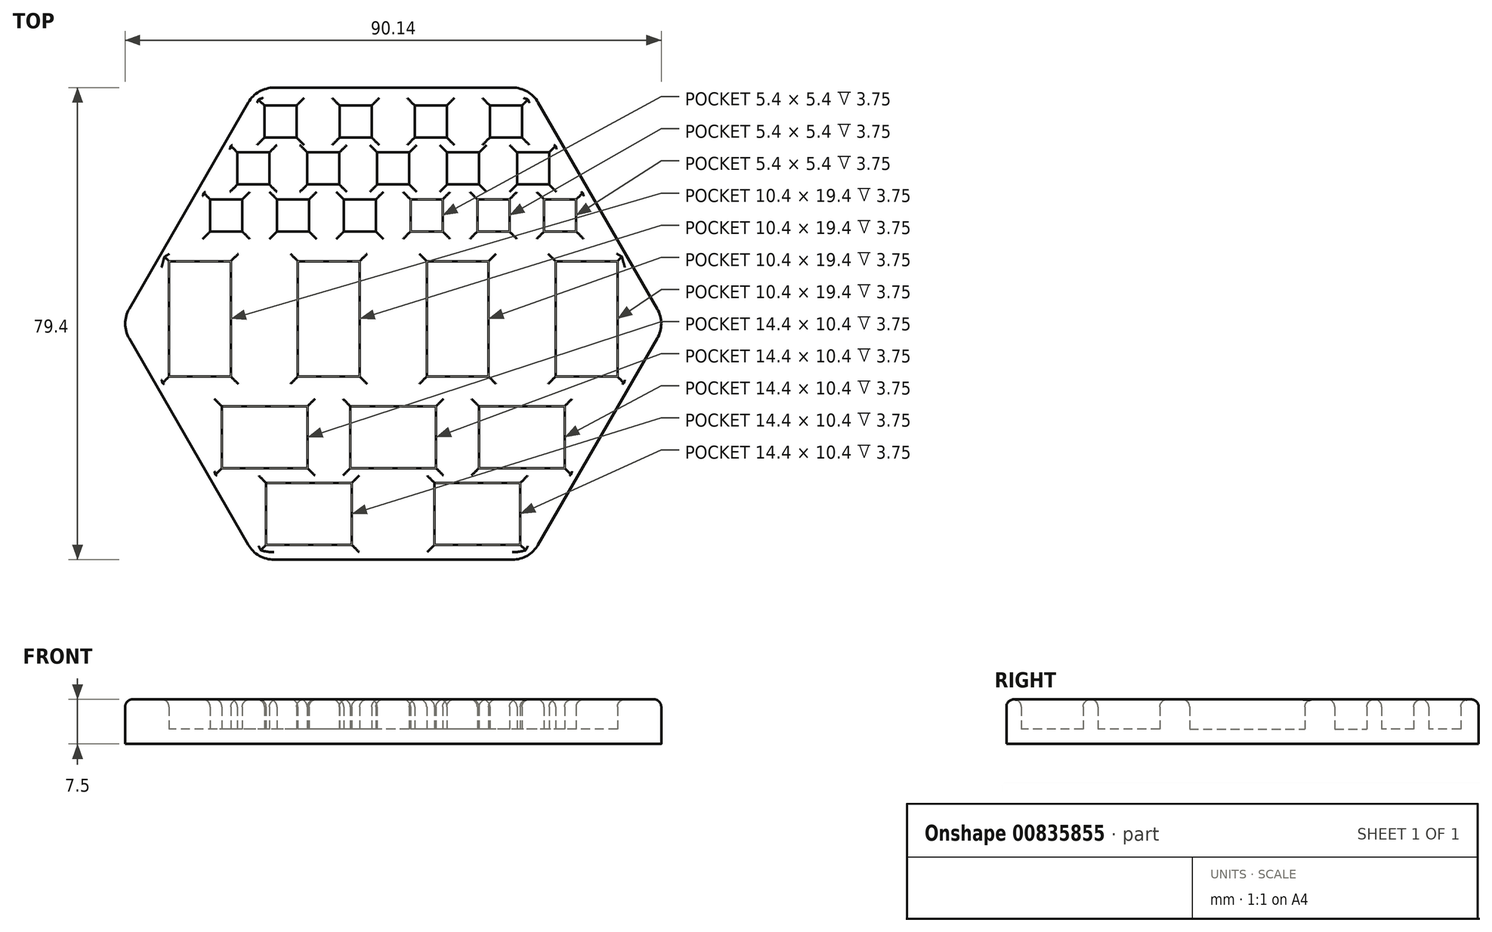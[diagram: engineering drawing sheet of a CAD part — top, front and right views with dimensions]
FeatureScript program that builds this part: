
annotation { "Feature Type Name" : "Feature", "Feature Type Description" : "" }
export const myFeature = defineFeature(function(context is Context, id is Id, definition is map)
    precondition{}
    {
        {
            var Q0;
            Q0=qCreatedBy(makeId("Top.planeOp"),FACE);
            var sketch = newSketch(context, id + "F0", { "sketchPlane" : qUnion([Q0])});
            skCircle(sketch, "E0.cCircle", {"center": v(0, 0) * mm, "radius": 39.7 * mm, "construction": true});
            skLineSegment(sketch, "E0.0", {"start": v(22.92, 39.7) * mm, "end": v(45.84, 0) * mm});
            skLineSegment(sketch, "E0.1", {"start": v(45.84, 0) * mm, "end": v(22.92, -39.7) * mm});
            skLineSegment(sketch, "E0.2", {"start": v(22.92, -39.7) * mm, "end": v(-22.92, -39.7) * mm});
            skLineSegment(sketch, "E0.3", {"start": v(-22.92, -39.7) * mm, "end": v(-45.84, 0) * mm});
            skLineSegment(sketch, "E0.4", {"start": v(-45.84, 0) * mm, "end": v(-22.92, 39.7) * mm});
            skLineSegment(sketch, "E0.5", {"start": v(-22.92, 39.7) * mm, "end": v(22.92, 39.7) * mm});
            skPoint(sketch, "E0.0.midPoint", {"position": v(34.38, 19.85) * mm});
            skLineSegment(sketch, "E1.bottom", {"start": v(-16.25, 36.7) * mm, "end": v(-21.65, 36.7) * mm});
            skLineSegment(sketch, "E1.top", {"start": v(-16.25, 31.3) * mm, "end": v(-21.65, 31.3) * mm});
            skLineSegment(sketch, "E1.left", {"start": v(-16.25, 36.7) * mm, "end": v(-16.25, 31.3) * mm});
            skLineSegment(sketch, "E1.right", {"start": v(-21.65, 36.7) * mm, "end": v(-21.65, 31.3) * mm});
            skPoint(sketch, "E1.middle", {"position": v(-18.95, 34) * mm});
            skLineSegment(sketch, "E2", {"start": v(-21.65, 36.7) * mm, "end": v(-24.65, 36.7) * mm, "construction": true});
            skLineSegment(sketch, "E3.1.0.0", {"start": v(-3.62, 31.3) * mm, "end": v(-9.02, 31.3) * mm});
            skLineSegment(sketch, "E3.1.0.1", {"start": v(-3.62, 36.7) * mm, "end": v(-3.62, 31.3) * mm});
            skLineSegment(sketch, "E3.1.0.2", {"start": v(-3.62, 36.7) * mm, "end": v(-9.02, 36.7) * mm});
            skLineSegment(sketch, "E3.1.0.3", {"start": v(-9.02, 36.7) * mm, "end": v(-9.02, 31.3) * mm});
            skLineSegment(sketch, "E3.2.0.0", {"start": v(9.02, 31.3) * mm, "end": v(3.62, 31.3) * mm});
            skLineSegment(sketch, "E3.2.0.1", {"start": v(9.02, 36.7) * mm, "end": v(9.02, 31.3) * mm});
            skLineSegment(sketch, "E3.2.0.2", {"start": v(9.02, 36.7) * mm, "end": v(3.62, 36.7) * mm});
            skLineSegment(sketch, "E3.2.0.3", {"start": v(3.62, 36.7) * mm, "end": v(3.62, 31.3) * mm});
            skLineSegment(sketch, "E3.3.0.0", {"start": v(21.65, 31.3) * mm, "end": v(16.25, 31.3) * mm});
            skLineSegment(sketch, "E3.3.0.1", {"start": v(21.65, 36.7) * mm, "end": v(21.65, 31.3) * mm});
            skLineSegment(sketch, "E3.3.0.2", {"start": v(21.65, 36.7) * mm, "end": v(16.25, 36.7) * mm});
            skLineSegment(sketch, "E3.3.0.3", {"start": v(16.25, 36.7) * mm, "end": v(16.25, 31.3) * mm});
            skLineSegment(sketch, "E3.direction1", {"start": v(-21.65, 31.3) * mm, "end": v(-9.02, 31.3) * mm, "construction": true});
            skLineSegment(sketch, "E4", {"start": v(21.65, 36.7) * mm, "end": v(24.65, 36.7) * mm, "construction": true});
            skLineSegment(sketch, "E5.bottom", {"start": v(-20.81, 28.8) * mm, "end": v(-26.21, 28.8) * mm});
            skLineSegment(sketch, "E5.top", {"start": v(-20.81, 23.4) * mm, "end": v(-26.21, 23.4) * mm});
            skLineSegment(sketch, "E5.left", {"start": v(-20.81, 28.8) * mm, "end": v(-20.81, 23.4) * mm});
            skLineSegment(sketch, "E5.right", {"start": v(-26.21, 28.8) * mm, "end": v(-26.21, 23.4) * mm});
            skPoint(sketch, "E5.middle", {"position": v(-23.51, 26.1) * mm});
            skLineSegment(sketch, "E6", {"start": v(-26.21, 28.8) * mm, "end": v(-29.21, 28.8) * mm, "construction": true});
            skLineSegment(sketch, "E7.1.0.0", {"start": v(-14.46, 28.8) * mm, "end": v(-14.46, 23.4) * mm});
            skLineSegment(sketch, "E7.1.0.1", {"start": v(-9.06, 28.8) * mm, "end": v(-14.46, 28.8) * mm});
            skLineSegment(sketch, "E7.1.0.2", {"start": v(-9.06, 28.8) * mm, "end": v(-9.06, 23.4) * mm});
            skLineSegment(sketch, "E7.1.0.3", {"start": v(-9.06, 23.4) * mm, "end": v(-14.46, 23.4) * mm});
            skLineSegment(sketch, "E7.2.0.0", {"start": v(-2.7, 28.8) * mm, "end": v(-2.7, 23.4) * mm});
            skLineSegment(sketch, "E7.2.0.1", {"start": v(2.7, 28.8) * mm, "end": v(-2.7, 28.8) * mm});
            skLineSegment(sketch, "E7.2.0.2", {"start": v(2.7, 28.8) * mm, "end": v(2.7, 23.4) * mm});
            skLineSegment(sketch, "E7.2.0.3", {"start": v(2.7, 23.4) * mm, "end": v(-2.7, 23.4) * mm});
            skLineSegment(sketch, "E7.3.0.0", {"start": v(9.06, 28.8) * mm, "end": v(9.06, 23.4) * mm});
            skLineSegment(sketch, "E7.3.0.1", {"start": v(14.46, 28.8) * mm, "end": v(9.06, 28.8) * mm});
            skLineSegment(sketch, "E7.3.0.2", {"start": v(14.46, 28.8) * mm, "end": v(14.46, 23.4) * mm});
            skLineSegment(sketch, "E7.3.0.3", {"start": v(14.46, 23.4) * mm, "end": v(9.06, 23.4) * mm});
            skLineSegment(sketch, "E7.4.0.0", {"start": v(20.81, 28.8) * mm, "end": v(20.81, 23.4) * mm});
            skLineSegment(sketch, "E7.4.0.1", {"start": v(26.21, 28.8) * mm, "end": v(20.81, 28.8) * mm});
            skLineSegment(sketch, "E7.4.0.2", {"start": v(26.21, 28.8) * mm, "end": v(26.21, 23.4) * mm});
            skLineSegment(sketch, "E7.4.0.3", {"start": v(26.21, 23.4) * mm, "end": v(20.81, 23.4) * mm});
            skLineSegment(sketch, "E7.direction1", {"start": v(-26.21, 23.4) * mm, "end": v(-14.46, 23.4) * mm, "construction": true});
            skLineSegment(sketch, "E8", {"start": v(26.21, 28.8) * mm, "end": v(29.21, 28.8) * mm, "construction": true});
            skLineSegment(sketch, "E9.bottom", {"start": v(-25.37, 15.5) * mm, "end": v(-30.77, 15.5) * mm});
            skLineSegment(sketch, "E9.top", {"start": v(-25.37, 20.9) * mm, "end": v(-30.77, 20.9) * mm});
            skLineSegment(sketch, "E9.left", {"start": v(-25.37, 15.5) * mm, "end": v(-25.37, 20.9) * mm});
            skLineSegment(sketch, "E9.right", {"start": v(-30.77, 15.5) * mm, "end": v(-30.77, 20.9) * mm});
            skPoint(sketch, "E9.middle", {"position": v(-28.07, 18.2) * mm});
            skLineSegment(sketch, "E10", {"start": v(-30.77, 20.9) * mm, "end": v(-33.77, 20.9) * mm, "construction": true});
            skLineSegment(sketch, "E11.1.0.0", {"start": v(-14.14, 20.9) * mm, "end": v(-19.54, 20.9) * mm});
            skLineSegment(sketch, "E11.1.0.1", {"start": v(-19.54, 15.5) * mm, "end": v(-19.54, 20.9) * mm});
            skLineSegment(sketch, "E11.1.0.2", {"start": v(-14.14, 15.5) * mm, "end": v(-19.54, 15.5) * mm});
            skLineSegment(sketch, "E11.1.0.3", {"start": v(-14.14, 15.5) * mm, "end": v(-14.14, 20.9) * mm});
            skLineSegment(sketch, "E11.2.0.0", {"start": v(-2.91, 20.9) * mm, "end": v(-8.31, 20.9) * mm});
            skLineSegment(sketch, "E11.2.0.1", {"start": v(-8.31, 15.5) * mm, "end": v(-8.31, 20.9) * mm});
            skLineSegment(sketch, "E11.2.0.2", {"start": v(-2.91, 15.5) * mm, "end": v(-8.31, 15.5) * mm});
            skLineSegment(sketch, "E11.2.0.3", {"start": v(-2.91, 15.5) * mm, "end": v(-2.91, 20.9) * mm});
            skLineSegment(sketch, "E11.3.0.0", {"start": v(8.31, 20.9) * mm, "end": v(2.91, 20.9) * mm});
            skLineSegment(sketch, "E11.3.0.1", {"start": v(2.91, 15.5) * mm, "end": v(2.91, 20.9) * mm});
            skLineSegment(sketch, "E11.3.0.2", {"start": v(8.31, 15.5) * mm, "end": v(2.91, 15.5) * mm});
            skLineSegment(sketch, "E11.3.0.3", {"start": v(8.31, 15.5) * mm, "end": v(8.31, 20.9) * mm});
            skLineSegment(sketch, "E11.4.0.0", {"start": v(19.54, 20.9) * mm, "end": v(14.14, 20.9) * mm});
            skLineSegment(sketch, "E11.4.0.1", {"start": v(14.14, 15.5) * mm, "end": v(14.14, 20.9) * mm});
            skLineSegment(sketch, "E11.4.0.2", {"start": v(19.54, 15.5) * mm, "end": v(14.14, 15.5) * mm});
            skLineSegment(sketch, "E11.4.0.3", {"start": v(19.54, 15.5) * mm, "end": v(19.54, 20.9) * mm});
            skLineSegment(sketch, "E11.5.0.0", {"start": v(30.77, 20.9) * mm, "end": v(25.37, 20.9) * mm});
            skLineSegment(sketch, "E11.5.0.1", {"start": v(25.37, 15.5) * mm, "end": v(25.37, 20.9) * mm});
            skLineSegment(sketch, "E11.5.0.2", {"start": v(30.77, 15.5) * mm, "end": v(25.37, 15.5) * mm});
            skLineSegment(sketch, "E11.5.0.3", {"start": v(30.77, 15.5) * mm, "end": v(30.77, 20.9) * mm});
            skLineSegment(sketch, "E11.direction1", {"start": v(-30.77, 20.9) * mm, "end": v(-19.54, 20.9) * mm, "construction": true});
            skLineSegment(sketch, "E12", {"start": v(30.77, 20.9) * mm, "end": v(33.77, 20.9) * mm, "construction": true});
            skLineSegment(sketch, "E13.bottom", {"start": v(-27.3, -8.9) * mm, "end": v(-37.7, -8.9) * mm});
            skLineSegment(sketch, "E13.top", {"start": v(-27.3, 10.5) * mm, "end": v(-37.7, 10.5) * mm});
            skLineSegment(sketch, "E13.left", {"start": v(-27.3, -8.9) * mm, "end": v(-27.3, 10.5) * mm});
            skLineSegment(sketch, "E13.right", {"start": v(-37.7, -8.9) * mm, "end": v(-37.7, 10.5) * mm});
            skPoint(sketch, "E13.middle", {"position": v(-32.5, 0.8) * mm});
            skLineSegment(sketch, "E14", {"start": v(-37.7, -8.9) * mm, "end": v(-40.7, -8.9) * mm, "construction": true});
            skLineSegment(sketch, "E15.1.0.0", {"start": v(-5.63, 10.5) * mm, "end": v(-16.03, 10.5) * mm});
            skLineSegment(sketch, "E15.1.0.1", {"start": v(-5.63, -8.9) * mm, "end": v(-5.63, 10.5) * mm});
            skLineSegment(sketch, "E15.1.0.2", {"start": v(-5.63, -8.9) * mm, "end": v(-16.03, -8.9) * mm});
            skLineSegment(sketch, "E15.1.0.3", {"start": v(-16.03, -8.9) * mm, "end": v(-16.03, 10.5) * mm});
            skLineSegment(sketch, "E15.2.0.0", {"start": v(16.03, 10.5) * mm, "end": v(5.63, 10.5) * mm});
            skLineSegment(sketch, "E15.2.0.1", {"start": v(16.03, -8.9) * mm, "end": v(16.03, 10.5) * mm});
            skLineSegment(sketch, "E15.2.0.2", {"start": v(16.03, -8.9) * mm, "end": v(5.63, -8.9) * mm});
            skLineSegment(sketch, "E15.2.0.3", {"start": v(5.63, -8.9) * mm, "end": v(5.63, 10.5) * mm});
            skLineSegment(sketch, "E15.3.0.0", {"start": v(37.7, 10.5) * mm, "end": v(27.3, 10.5) * mm});
            skLineSegment(sketch, "E15.3.0.1", {"start": v(37.7, -8.9) * mm, "end": v(37.7, 10.5) * mm});
            skLineSegment(sketch, "E15.3.0.2", {"start": v(37.7, -8.9) * mm, "end": v(27.3, -8.9) * mm});
            skLineSegment(sketch, "E15.3.0.3", {"start": v(27.3, -8.9) * mm, "end": v(27.3, 10.5) * mm});
            skLineSegment(sketch, "E15.direction1", {"start": v(-37.7, 10.5) * mm, "end": v(-16.03, 10.5) * mm, "construction": true});
            skLineSegment(sketch, "E16", {"start": v(37.7, -8.9) * mm, "end": v(40.7, -8.9) * mm, "construction": true});
            skLineSegment(sketch, "E17.bottom", {"start": v(-14.41, -13.9) * mm, "end": v(-28.81, -13.9) * mm});
            skLineSegment(sketch, "E17.top", {"start": v(-14.41, -24.3) * mm, "end": v(-28.81, -24.3) * mm});
            skLineSegment(sketch, "E17.left", {"start": v(-14.41, -13.9) * mm, "end": v(-14.41, -24.3) * mm});
            skLineSegment(sketch, "E17.right", {"start": v(-28.81, -13.9) * mm, "end": v(-28.81, -24.3) * mm});
            skPoint(sketch, "E17.middle", {"position": v(-21.61, -19.1) * mm});
            skLineSegment(sketch, "E18", {"start": v(-28.81, -24.3) * mm, "end": v(-31.81, -24.3) * mm, "construction": true});
            skLineSegment(sketch, "E19.1.0.0", {"start": v(7.2, -24.3) * mm, "end": v(-7.2, -24.3) * mm});
            skLineSegment(sketch, "E19.1.0.1", {"start": v(-7.2, -13.9) * mm, "end": v(-7.2, -24.3) * mm});
            skLineSegment(sketch, "E19.1.0.2", {"start": v(7.2, -13.9) * mm, "end": v(-7.2, -13.9) * mm});
            skLineSegment(sketch, "E19.1.0.3", {"start": v(7.2, -13.9) * mm, "end": v(7.2, -24.3) * mm});
            skLineSegment(sketch, "E19.2.0.0", {"start": v(28.81, -24.3) * mm, "end": v(14.41, -24.3) * mm});
            skLineSegment(sketch, "E19.2.0.1", {"start": v(14.41, -13.9) * mm, "end": v(14.41, -24.3) * mm});
            skLineSegment(sketch, "E19.2.0.2", {"start": v(28.81, -13.9) * mm, "end": v(14.41, -13.9) * mm});
            skLineSegment(sketch, "E19.2.0.3", {"start": v(28.81, -13.9) * mm, "end": v(28.81, -24.3) * mm});
            skLineSegment(sketch, "E19.direction1", {"start": v(-28.81, -24.3) * mm, "end": v(-7.2, -24.3) * mm, "construction": true});
            skLineSegment(sketch, "E20", {"start": v(28.81, -24.3) * mm, "end": v(31.81, -24.3) * mm, "construction": true});
            skLineSegment(sketch, "E21.bottom", {"start": v(-6.96, -26.8) * mm, "end": v(-21.36, -26.8) * mm});
            skLineSegment(sketch, "E21.top", {"start": v(-6.96, -37.2) * mm, "end": v(-21.36, -37.2) * mm});
            skLineSegment(sketch, "E21.left", {"start": v(-6.96, -26.8) * mm, "end": v(-6.96, -37.2) * mm});
            skLineSegment(sketch, "E21.right", {"start": v(-21.36, -26.8) * mm, "end": v(-21.36, -37.2) * mm});
            skPoint(sketch, "E21.middle", {"position": v(-14.16, -32) * mm});
            skLineSegment(sketch, "E22", {"start": v(-21.36, -37.2) * mm, "end": v(-24.36, -37.2) * mm, "construction": true});
            skLineSegment(sketch, "E23.1.0.0", {"start": v(6.96, -26.8) * mm, "end": v(6.96, -37.2) * mm});
            skLineSegment(sketch, "E23.1.0.1", {"start": v(21.36, -26.8) * mm, "end": v(6.96, -26.8) * mm});
            skLineSegment(sketch, "E23.1.0.2", {"start": v(21.36, -26.8) * mm, "end": v(21.36, -37.2) * mm});
            skLineSegment(sketch, "E23.1.0.3", {"start": v(21.36, -37.2) * mm, "end": v(6.96, -37.2) * mm});
            skLineSegment(sketch, "E23.direction1", {"start": v(-21.36, -37.2) * mm, "end": v(6.96, -37.2) * mm, "construction": true});
            skLineSegment(sketch, "E24", {"start": v(21.36, -37.2) * mm, "end": v(24.36, -37.2) * mm, "construction": true});
            skSolve(sketch);
        }
        {
            var Q0;
            Q0=makeQuery(id+"F0.imprint","IMPRINT",FACE,{"disambiguationData":[TD([[makeQuery(id+"F0.imprint","IMPRINT",EDGE,{"derivedFrom":sQuery(id+"F0.wireOp",EDGE,"E0.0")}),-1.0]])]});
            extrude(context, id + "F1", {"entities" : qUnion([Q0]), "depth" : 7.5 * mm, "offsetDistance" : 25 * mm});
        }
        {
            var Q0;
            Q0=makeQuery(id+"F0.imprint","IMPRINT",FACE,{"disambiguationData":[TD([[makeQuery(id+"F0.imprint","IMPRINT",EDGE,{"derivedFrom":sQuery(id+"F0.wireOp",EDGE,"E13.bottom")}),-1.0]])]});
            var Q1;
            Q1=makeQuery(id+"F0.imprint","IMPRINT",FACE,{"disambiguationData":[TD([[makeQuery(id+"F0.imprint","IMPRINT",EDGE,{"derivedFrom":sQuery(id+"F0.wireOp",EDGE,"E15.1.0.0")}),1.0]])]});
            var Q2;
            Q2=makeQuery(id+"F0.imprint","IMPRINT",FACE,{"disambiguationData":[TD([[makeQuery(id+"F0.imprint","IMPRINT",EDGE,{"derivedFrom":sQuery(id+"F0.wireOp",EDGE,"E15.2.0.0")}),1.0]])]});
            var Q3;
            Q3=makeQuery(id+"F0.imprint","IMPRINT",FACE,{"disambiguationData":[TD([[makeQuery(id+"F0.imprint","IMPRINT",EDGE,{"derivedFrom":sQuery(id+"F0.wireOp",EDGE,"E15.3.0.0")}),1.0]])]});
            var Q4;
            Q4=makeQuery(id+"F0.imprint","IMPRINT",FACE,{"disambiguationData":[TD([[makeQuery(id+"F0.imprint","IMPRINT",EDGE,{"derivedFrom":sQuery(id+"F0.wireOp",EDGE,"E11.5.0.0")}),1.0]])]});
            var Q5;
            Q5=makeQuery(id+"F0.imprint","IMPRINT",FACE,{"disambiguationData":[TD([[makeQuery(id+"F0.imprint","IMPRINT",EDGE,{"derivedFrom":sQuery(id+"F0.wireOp",EDGE,"E11.4.0.0")}),1.0]])]});
            var Q6;
            Q6=makeQuery(id+"F0.imprint","IMPRINT",FACE,{"disambiguationData":[TD([[makeQuery(id+"F0.imprint","IMPRINT",EDGE,{"derivedFrom":sQuery(id+"F0.wireOp",EDGE,"E11.3.0.0")}),1.0]])]});
            var Q7;
            Q7=makeQuery(id+"F0.imprint","IMPRINT",FACE,{"disambiguationData":[TD([[makeQuery(id+"F0.imprint","IMPRINT",EDGE,{"derivedFrom":sQuery(id+"F0.wireOp",EDGE,"E11.2.0.0")}),1.0]])]});
            var Q8;
            Q8=makeQuery(id+"F0.imprint","IMPRINT",FACE,{"disambiguationData":[TD([[makeQuery(id+"F0.imprint","IMPRINT",EDGE,{"derivedFrom":sQuery(id+"F0.wireOp",EDGE,"E11.1.0.0")}),1.0]])]});
            var Q9;
            Q9=makeQuery(id+"F0.imprint","IMPRINT",FACE,{"disambiguationData":[TD([[makeQuery(id+"F0.imprint","IMPRINT",EDGE,{"derivedFrom":sQuery(id+"F0.wireOp",EDGE,"E9.bottom")}),-1.0]])]});
            var Q10;
            Q10=makeQuery(id+"F0.imprint","IMPRINT",FACE,{"disambiguationData":[TD([[makeQuery(id+"F0.imprint","IMPRINT",EDGE,{"derivedFrom":sQuery(id+"F0.wireOp",EDGE,"E5.bottom")}),1.0]])]});
            var Q11;
            Q11=makeQuery(id+"F0.imprint","IMPRINT",FACE,{"disambiguationData":[TD([[makeQuery(id+"F0.imprint","IMPRINT",EDGE,{"derivedFrom":sQuery(id+"F0.wireOp",EDGE,"E7.1.0.0")}),1.0]])]});
            var Q12;
            Q12=makeQuery(id+"F0.imprint","IMPRINT",FACE,{"disambiguationData":[TD([[makeQuery(id+"F0.imprint","IMPRINT",EDGE,{"derivedFrom":sQuery(id+"F0.wireOp",EDGE,"E7.2.0.0")}),1.0]])]});
            var Q13;
            Q13=makeQuery(id+"F0.imprint","IMPRINT",FACE,{"disambiguationData":[TD([[makeQuery(id+"F0.imprint","IMPRINT",EDGE,{"derivedFrom":sQuery(id+"F0.wireOp",EDGE,"E7.3.0.0")}),1.0]])]});
            var Q14;
            Q14=makeQuery(id+"F0.imprint","IMPRINT",FACE,{"disambiguationData":[TD([[makeQuery(id+"F0.imprint","IMPRINT",EDGE,{"derivedFrom":sQuery(id+"F0.wireOp",EDGE,"E7.4.0.0")}),1.0]])]});
            var Q15;
            Q15=makeQuery(id+"F0.imprint","IMPRINT",FACE,{"disambiguationData":[TD([[makeQuery(id+"F0.imprint","IMPRINT",EDGE,{"derivedFrom":sQuery(id+"F0.wireOp",EDGE,"E3.3.0.0")}),-1.0]])]});
            var Q16;
            Q16=makeQuery(id+"F0.imprint","IMPRINT",FACE,{"disambiguationData":[TD([[makeQuery(id+"F0.imprint","IMPRINT",EDGE,{"derivedFrom":sQuery(id+"F0.wireOp",EDGE,"E3.2.0.0")}),-1.0]])]});
            var Q17;
            Q17=makeQuery(id+"F0.imprint","IMPRINT",FACE,{"disambiguationData":[TD([[makeQuery(id+"F0.imprint","IMPRINT",EDGE,{"derivedFrom":sQuery(id+"F0.wireOp",EDGE,"E3.1.0.0")}),-1.0]])]});
            var Q18;
            Q18=makeQuery(id+"F0.imprint","IMPRINT",FACE,{"disambiguationData":[TD([[makeQuery(id+"F0.imprint","IMPRINT",EDGE,{"derivedFrom":sQuery(id+"F0.wireOp",EDGE,"E1.bottom")}),1.0]])]});
            var Q19;
            Q19=makeQuery(id+"F0.imprint","IMPRINT",FACE,{"disambiguationData":[TD([[makeQuery(id+"F0.imprint","IMPRINT",EDGE,{"derivedFrom":sQuery(id+"F0.wireOp",EDGE,"E17.bottom")}),1.0]])]});
            var Q20;
            Q20=makeQuery(id+"F0.imprint","IMPRINT",FACE,{"disambiguationData":[TD([[makeQuery(id+"F0.imprint","IMPRINT",EDGE,{"derivedFrom":sQuery(id+"F0.wireOp",EDGE,"E19.1.0.0")}),-1.0]])]});
            var Q21;
            Q21=makeQuery(id+"F0.imprint","IMPRINT",FACE,{"disambiguationData":[TD([[makeQuery(id+"F0.imprint","IMPRINT",EDGE,{"derivedFrom":sQuery(id+"F0.wireOp",EDGE,"E19.2.0.0")}),-1.0]])]});
            var Q22;
            Q22=makeQuery(id+"F0.imprint","IMPRINT",FACE,{"disambiguationData":[TD([[makeQuery(id+"F0.imprint","IMPRINT",EDGE,{"derivedFrom":sQuery(id+"F0.wireOp",EDGE,"E23.1.0.0")}),1.0]])]});
            var Q23;
            Q23=makeQuery(id+"F0.imprint","IMPRINT",FACE,{"disambiguationData":[TD([[makeQuery(id+"F0.imprint","IMPRINT",EDGE,{"derivedFrom":sQuery(id+"F0.wireOp",EDGE,"E21.bottom")}),1.0]])]});
            extrude(context, id + "F2", {"entities" : qUnion([Q0, Q1, Q2, Q3, Q4, Q5, Q6, Q7, Q8, Q9, Q10, Q11, Q12, Q13, Q14, Q15, Q16, Q17, Q18, Q19, Q20, Q21, Q22, Q23]), "operationType" : NewBodyOperationType.ADD, "depth" : 2.5 * mm, "offsetDistance" : 25 * mm});
        }
        {
            var Q0;
            Q0=makeQuery(id+"F1.opExtrude","SWEPT_EDGE",EDGE,{"disambiguationData":[OSD([sQuery(id+"F0.wireOp",EDGE,"E0.0"),sQuery(id+"F0.wireOp",EDGE,"E0.5")])]});
            var Q1;
            Q1=makeQuery(id+"F1.opExtrude","SWEPT_EDGE",EDGE,{"disambiguationData":[OSD([sQuery(id+"F0.wireOp",EDGE,"E0.4"),sQuery(id+"F0.wireOp",EDGE,"E0.5")])]});
            var Q2;
            Q2=makeQuery(id+"F1.opExtrude","SWEPT_EDGE",EDGE,{"disambiguationData":[OSD([sQuery(id+"F0.wireOp",EDGE,"E0.3"),sQuery(id+"F0.wireOp",EDGE,"E0.4")])]});
            var Q3;
            Q3=makeQuery(id+"F1.opExtrude","SWEPT_EDGE",EDGE,{"disambiguationData":[OSD([sQuery(id+"F0.wireOp",EDGE,"E0.2"),sQuery(id+"F0.wireOp",EDGE,"E0.3")])]});
            var Q4;
            Q4=makeQuery(id+"F1.opExtrude","SWEPT_EDGE",EDGE,{"disambiguationData":[OSD([sQuery(id+"F0.wireOp",EDGE,"E0.0"),sQuery(id+"F0.wireOp",EDGE,"E0.1")])]});
            var Q5;
            Q5=makeQuery(id+"F1.opExtrude","SWEPT_EDGE",EDGE,{"disambiguationData":[OSD([sQuery(id+"F0.wireOp",EDGE,"E0.1"),sQuery(id+"F0.wireOp",EDGE,"E0.2")])]});
            fillet(context, id + "F3", {"entities" : qUnion([Q0, Q1, Q2, Q3, Q4, Q5]), "radius" : 5 * mm, "tangentPropagation" : true, "allowEdgeOverflow" : false});
        }
        {
            var Q0;
            Q0=makeQuery(id+"F1.opExtrude","CAP_FACE",FACE,{"disambiguationData":[OSD([sQuery(id+"F0.wireOp",EDGE,"E0.0"),sQuery(id+"F0.wireOp",EDGE,"E0.1"),sQuery(id+"F0.wireOp",EDGE,"E0.2"),sQuery(id+"F0.wireOp",EDGE,"E0.3"),sQuery(id+"F0.wireOp",EDGE,"E0.4"),sQuery(id+"F0.wireOp",EDGE,"E0.5"),sQuery(id+"F0.wireOp",EDGE,"E1.bottom"),sQuery(id+"F0.wireOp",EDGE,"E1.top"),sQuery(id+"F0.wireOp",EDGE,"E1.left"),sQuery(id+"F0.wireOp",EDGE,"E1.right"),sQuery(id+"F0.wireOp",EDGE,"E3.1.0.0"),sQuery(id+"F0.wireOp",EDGE,"E3.1.0.1"),sQuery(id+"F0.wireOp",EDGE,"E3.1.0.2"),sQuery(id+"F0.wireOp",EDGE,"E3.1.0.3"),sQuery(id+"F0.wireOp",EDGE,"E3.2.0.0"),sQuery(id+"F0.wireOp",EDGE,"E3.2.0.1"),sQuery(id+"F0.wireOp",EDGE,"E3.2.0.2"),sQuery(id+"F0.wireOp",EDGE,"E3.2.0.3"),sQuery(id+"F0.wireOp",EDGE,"E3.3.0.0"),sQuery(id+"F0.wireOp",EDGE,"E3.3.0.1"),sQuery(id+"F0.wireOp",EDGE,"E3.3.0.2"),sQuery(id+"F0.wireOp",EDGE,"E3.3.0.3"),sQuery(id+"F0.wireOp",EDGE,"E5.bottom"),sQuery(id+"F0.wireOp",EDGE,"E5.top"),sQuery(id+"F0.wireOp",EDGE,"E5.left"),sQuery(id+"F0.wireOp",EDGE,"E5.right"),sQuery(id+"F0.wireOp",EDGE,"E7.1.0.0"),sQuery(id+"F0.wireOp",EDGE,"E7.1.0.1"),sQuery(id+"F0.wireOp",EDGE,"E7.1.0.2"),sQuery(id+"F0.wireOp",EDGE,"E7.1.0.3"),sQuery(id+"F0.wireOp",EDGE,"E7.2.0.0"),sQuery(id+"F0.wireOp",EDGE,"E7.2.0.1"),sQuery(id+"F0.wireOp",EDGE,"E7.2.0.2"),sQuery(id+"F0.wireOp",EDGE,"E7.2.0.3"),sQuery(id+"F0.wireOp",EDGE,"E7.3.0.0"),sQuery(id+"F0.wireOp",EDGE,"E7.3.0.1"),sQuery(id+"F0.wireOp",EDGE,"E7.3.0.2"),sQuery(id+"F0.wireOp",EDGE,"E7.3.0.3"),sQuery(id+"F0.wireOp",EDGE,"E7.4.0.0"),sQuery(id+"F0.wireOp",EDGE,"E7.4.0.1"),sQuery(id+"F0.wireOp",EDGE,"E7.4.0.2"),sQuery(id+"F0.wireOp",EDGE,"E7.4.0.3"),sQuery(id+"F0.wireOp",EDGE,"E9.bottom"),sQuery(id+"F0.wireOp",EDGE,"E9.top"),sQuery(id+"F0.wireOp",EDGE,"E9.left"),sQuery(id+"F0.wireOp",EDGE,"E9.right"),sQuery(id+"F0.wireOp",EDGE,"E11.1.0.0"),sQuery(id+"F0.wireOp",EDGE,"E11.1.0.1"),sQuery(id+"F0.wireOp",EDGE,"E11.1.0.2"),sQuery(id+"F0.wireOp",EDGE,"E11.1.0.3"),sQuery(id+"F0.wireOp",EDGE,"E11.2.0.0"),sQuery(id+"F0.wireOp",EDGE,"E11.2.0.1"),sQuery(id+"F0.wireOp",EDGE,"E11.2.0.2"),sQuery(id+"F0.wireOp",EDGE,"E11.2.0.3"),sQuery(id+"F0.wireOp",EDGE,"E11.3.0.0"),sQuery(id+"F0.wireOp",EDGE,"E11.3.0.1"),sQuery(id+"F0.wireOp",EDGE,"E11.3.0.2"),sQuery(id+"F0.wireOp",EDGE,"E11.3.0.3"),sQuery(id+"F0.wireOp",EDGE,"E11.4.0.0"),sQuery(id+"F0.wireOp",EDGE,"E11.4.0.1"),sQuery(id+"F0.wireOp",EDGE,"E11.4.0.2"),sQuery(id+"F0.wireOp",EDGE,"E11.4.0.3"),sQuery(id+"F0.wireOp",EDGE,"E11.5.0.0"),sQuery(id+"F0.wireOp",EDGE,"E11.5.0.1"),sQuery(id+"F0.wireOp",EDGE,"E11.5.0.2"),sQuery(id+"F0.wireOp",EDGE,"E11.5.0.3"),sQuery(id+"F0.wireOp",EDGE,"E13.bottom"),sQuery(id+"F0.wireOp",EDGE,"E13.top"),sQuery(id+"F0.wireOp",EDGE,"E13.left"),sQuery(id+"F0.wireOp",EDGE,"E13.right"),sQuery(id+"F0.wireOp",EDGE,"E15.1.0.0"),sQuery(id+"F0.wireOp",EDGE,"E15.1.0.1"),sQuery(id+"F0.wireOp",EDGE,"E15.1.0.2"),sQuery(id+"F0.wireOp",EDGE,"E15.1.0.3"),sQuery(id+"F0.wireOp",EDGE,"E15.2.0.0"),sQuery(id+"F0.wireOp",EDGE,"E15.2.0.1"),sQuery(id+"F0.wireOp",EDGE,"E15.2.0.2"),sQuery(id+"F0.wireOp",EDGE,"E15.2.0.3"),sQuery(id+"F0.wireOp",EDGE,"E15.3.0.0"),sQuery(id+"F0.wireOp",EDGE,"E15.3.0.1"),sQuery(id+"F0.wireOp",EDGE,"E15.3.0.2"),sQuery(id+"F0.wireOp",EDGE,"E15.3.0.3"),sQuery(id+"F0.wireOp",EDGE,"E17.bottom"),sQuery(id+"F0.wireOp",EDGE,"E17.top"),sQuery(id+"F0.wireOp",EDGE,"E17.left"),sQuery(id+"F0.wireOp",EDGE,"E17.right"),sQuery(id+"F0.wireOp",EDGE,"E19.1.0.0"),sQuery(id+"F0.wireOp",EDGE,"E19.1.0.1"),sQuery(id+"F0.wireOp",EDGE,"E19.1.0.2"),sQuery(id+"F0.wireOp",EDGE,"E19.1.0.3"),sQuery(id+"F0.wireOp",EDGE,"E19.2.0.0"),sQuery(id+"F0.wireOp",EDGE,"E19.2.0.1"),sQuery(id+"F0.wireOp",EDGE,"E19.2.0.2"),sQuery(id+"F0.wireOp",EDGE,"E19.2.0.3"),sQuery(id+"F0.wireOp",EDGE,"E21.bottom"),sQuery(id+"F0.wireOp",EDGE,"E21.top"),sQuery(id+"F0.wireOp",EDGE,"E21.left"),sQuery(id+"F0.wireOp",EDGE,"E21.right"),sQuery(id+"F0.wireOp",EDGE,"E23.1.0.0"),sQuery(id+"F0.wireOp",EDGE,"E23.1.0.1"),sQuery(id+"F0.wireOp",EDGE,"E23.1.0.2"),sQuery(id+"F0.wireOp",EDGE,"E23.1.0.3")])],"isStart":false});
            fillet(context, id + "F4", {"entities" : qUnion([Q0]), "radius" : 1.25 * mm, "tangentPropagation" : true, "allowEdgeOverflow" : false});
        }
    });
